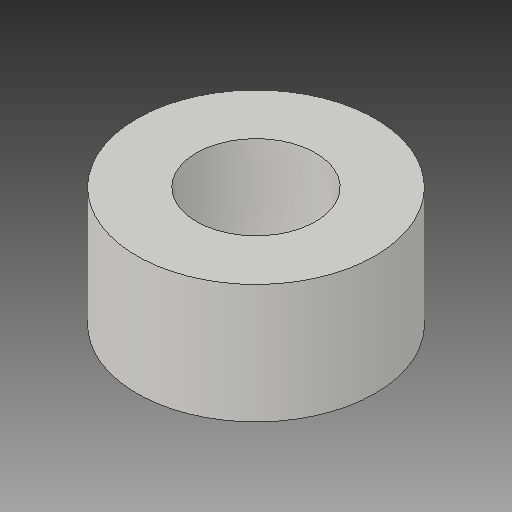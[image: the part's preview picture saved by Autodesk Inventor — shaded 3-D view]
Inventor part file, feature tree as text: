
AUTODESK INVENTOR PART (.ipt)
format: ipt  version: 2017 (Build 210142000, 142)  size: 94,720 bytes
history: native  units: in
note: dims shown in document units (in); Inventor stores cm internally (conversion verified against a paired STEP export)
features: extrude x1, sketch x1
ambient origin geometry x8: Origin, YZ Plane, XZ Plane, XY Plane, X Axis, Y Axis, Z Axis, Center Point
bodies: Solid1 (feature_tree)
feature tree (2):
  extrude  "Extrusion1"  Depth=0.25in
  sketch  "Sketch1"  dims[d0=0.25in d1=0.5in d2=0.25in d3=0.0in]
